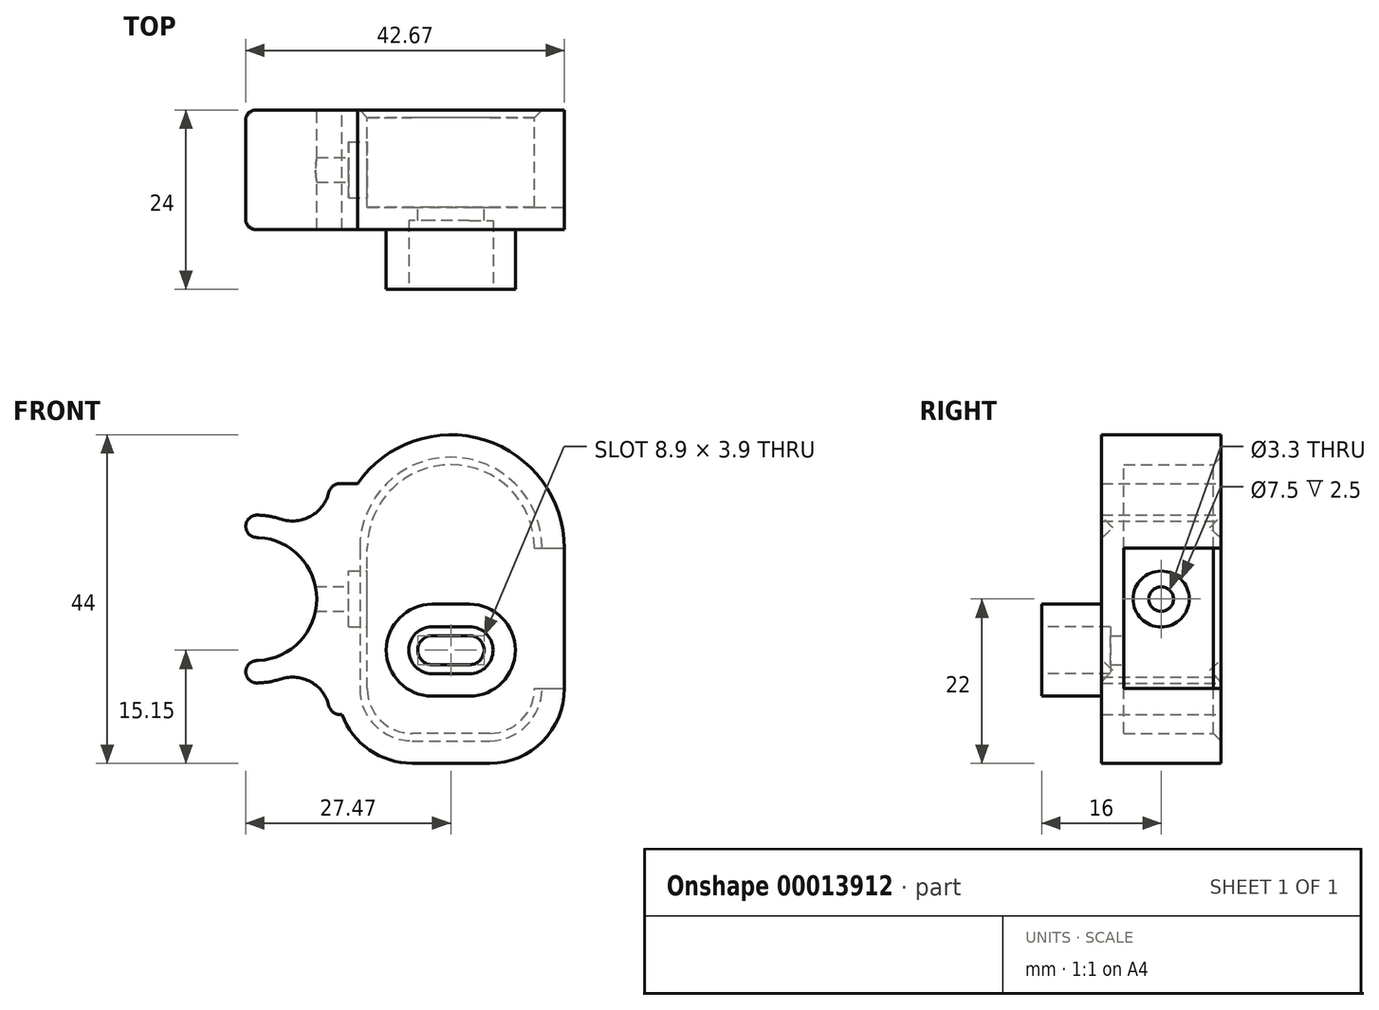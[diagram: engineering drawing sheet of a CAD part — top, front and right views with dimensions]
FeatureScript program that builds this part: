
annotation { "Feature Type Name" : "Feature", "Feature Type Description" : "" }
export const myFeature = defineFeature(function(context is Context, id is Id, definition is map)
    precondition{}
    {
        {
            var Q0;
            Q0=qCreatedBy(makeId("Front.planeOp"),FACE);
            var sketch = newSketch(context, id + "F0", { "sketchPlane" : qUnion([Q0])});
            skArc(sketch, "E0", {"start": v(-1.08, -8.18) * mm, "mid": v(8.25, 0) * mm, "end": v(-1.08, 8.18) * mm});
            skArc(sketch, "E1", {"start": v(3.46, 10.7) * mm, "mid": v(1.02, 11.2) * mm, "end": v(-1.47, 11.15) * mm});
            skLineSegment(sketch, "E2", {"start": v(-1.08, 8.18) * mm, "end": v(-1.47, 11.15) * mm});
            skLineSegment(sketch, "E3", {"start": v(-1.08, -8.18) * mm, "end": v(-1.47, -11.15) * mm});
            skLineSegment(sketch, "E4", {"start": v(0, 0) * mm, "end": v(-11.25, 0) * mm, "construction": true});
            skLineSegment(sketch, "E5", {"start": v(10, 15.46) * mm, "end": v(10, 15.46) * mm});
            skLineSegment(sketch, "E6", {"start": v(15, 0) * mm, "end": v(15, 15.46) * mm});
            skPoint(sketch, "E7.orphan", {"position": v(8.25, 0) * mm});
            skArc(sketch, "E8.trimOffspring", {"start": v(-1.47, -11.15) * mm, "mid": v(1.02, -11.2) * mm, "end": v(3.46, -10.7) * mm});
            skArc(sketch, "E9.filletArc", {"start": v(3.46, 10.7) * mm, "mid": v(7.94, 11.42) * mm, "end": v(10, 15.46) * mm});
            skLineSegment(sketch, "E10.MirrorCS", {"start": v(15, 0) * mm, "end": v(15, -15.46) * mm});
            skLineSegment(sketch, "E11", {"start": v(10, 15.46) * mm, "end": v(15, 15.46) * mm});
            skLineSegment(sketch, "E12.MirrorCS", {"start": v(10, -15.46) * mm, "end": v(15, -15.46) * mm});
            skArc(sketch, "E13.MirrorCS", {"start": v(3.46, -10.7) * mm, "mid": v(7.94, -11.42) * mm, "end": v(10, -15.46) * mm});
            skSolve(sketch);
        }
        {
            var Q0;
            Q0=qSketchRegion(id+"F0",true);
            extrude(context, id + "F1", {"entities" : qUnion([Q0]), "depth" : 8 * mm, "hasSecondDirection" : true, "secondDirectionOppositeDirection" : true, "secondDirectionDepth" : 8 * mm});
        }
        {
            var Q0;
            Q0=makeQuery(id+"F1.opExtrude","SWEPT_FACE",FACE,{"disambiguationData":[OSD([sQuery(id+"F0.wireOp",EDGE,"E6"),sQuery(id+"F0.wireOp",EDGE,"E10.MirrorCS")])]});
            var sketch = newSketch(context, id + "F2", { "sketchPlane" : qUnion([Q0])});
            skCircle(sketch, "E14", {"center": v(0, 0) * mm, "radius": 4 * mm});
            skSolve(sketch);
        }
        {
            var Q0;
            Q0=qSketchRegion(id+"F2",true);
            extrude(context, id + "F3", {"entities" : qUnion([Q0]), "operationType" : NewBodyOperationType.REMOVE, "oppositeDirection" : true, "depth" : 3 * mm});
        }
        {
            var Q0;
            Q0=makeQuery(id+"F1.opExtrude","SWEPT_FACE",FACE,{"disambiguationData":[OSD([sQuery(id+"F0.wireOp",EDGE,"E3")])]});
            var Q1;
            Q1=makeQuery(id+"F1.opExtrude","SWEPT_FACE",FACE,{"disambiguationData":[OSD([sQuery(id+"F0.wireOp",EDGE,"E2")])]});
            var Q2;
            Q2=makeQuery(id+"F1.opExtrude","SWEPT_EDGE",EDGE,{"disambiguationData":[OSD([sQuery(id+"F0.wireOp",EDGE,"E9.filletArc"),sQuery(id+"F0.wireOp",EDGE,"E11")])]});
            var Q3;
            Q3=makeQuery(id+"F1.opExtrude","SWEPT_EDGE",EDGE,{"disambiguationData":[OSD([sQuery(id+"F0.wireOp",EDGE,"E12.MirrorCS"),sQuery(id+"F0.wireOp",EDGE,"E13.MirrorCS")])]});
            fillet(context, id + "F4", {"entities" : qUnion([Q0, Q1, Q2, Q3]), "radius" : 1.5 * mm, "tangentPropagation" : true, "allowEdgeOverflow" : false});
        }
        {
            var Q0;
            Q0=qCreatedBy(makeId("Front.planeOp"),FACE);
            var sketch = newSketch(context, id + "F5", { "sketchPlane" : qUnion([Q0])});
            skLineSegment(sketch, "E15.1", {"start": v(15, 6.8) * mm, "end": v(15, -12) * mm});
            skArc(sketch, "E16", {"start": v(15, 6.8) * mm, "mid": v(26.2, 18) * mm, "end": v(37.4, 6.8) * mm});
            skArc(sketch, "E17", {"start": v(15, -12) * mm, "mid": v(16.76, -16.24) * mm, "end": v(21, -18) * mm});
            skLineSegment(sketch, "E18", {"start": v(21, -18) * mm, "end": v(31.4, -18) * mm});
            skArc(sketch, "E19", {"start": v(31.4, -18) * mm, "mid": v(35.64, -16.24) * mm, "end": v(37.4, -12) * mm});
            skLineSegment(sketch, "E20", {"start": v(26.2, 18) * mm, "end": v(0, 18) * mm, "construction": true});
            skLineSegment(sketch, "E21", {"start": v(0, 0) * mm, "end": v(15, 0) * mm, "construction": true});
            skArc(sketch, "E22.0", {"start": v(11, 6.8) * mm, "mid": v(26.2, 22) * mm, "end": v(41.4, 6.8) * mm});
            skLineSegment(sketch, "E23", {"start": v(37.4, 6.8) * mm, "end": v(41.4, 6.8) * mm});
            skArc(sketch, "E24.0", {"start": v(31.4, -22) * mm, "mid": v(38.47, -19.07) * mm, "end": v(41.4, -12) * mm});
            skLineSegment(sketch, "E24.1", {"start": v(21, -22) * mm, "end": v(31.4, -22) * mm});
            skArc(sketch, "E24.2", {"start": v(11, -12) * mm, "mid": v(13.93, -19.07) * mm, "end": v(21, -22) * mm});
            skLineSegment(sketch, "E25", {"start": v(11, 6.8) * mm, "end": v(11, -12) * mm});
            skLineSegment(sketch, "E26", {"start": v(37.4, -12) * mm, "end": v(41.4, -12) * mm});
            skSolve(sketch);
        }
        {
            var Q0;
            Q0 = qSketchRegion(id + "F5", true);
            var Q1;
            Q1=makeQuery(id+"F1.opExtrude","CAP_FACE",FACE,{"disambiguationData":[OSD([sQuery(id+"F0.wireOp",EDGE,"E0"),sQuery(id+"F0.wireOp",EDGE,"E1"),sQuery(id+"F0.wireOp",EDGE,"E2"),sQuery(id+"F0.wireOp",EDGE,"E3"),sQuery(id+"F0.wireOp",EDGE,"E6"),sQuery(id+"F0.wireOp",EDGE,"E8.trimOffspring"),sQuery(id+"F0.wireOp",EDGE,"E9.filletArc"),sQuery(id+"F0.wireOp",EDGE,"E10.MirrorCS"),sQuery(id+"F0.wireOp",EDGE,"E11"),sQuery(id+"F0.wireOp",EDGE,"E12.MirrorCS"),sQuery(id+"F0.wireOp",EDGE,"E13.MirrorCS")])],"isStart":false});
            var Q2;
            Q2=makeQuery(id+"F1.opExtrude","CAP_FACE",FACE,{"disambiguationData":[OSD([sQuery(id+"F0.wireOp",EDGE,"E0"),sQuery(id+"F0.wireOp",EDGE,"E1"),sQuery(id+"F0.wireOp",EDGE,"E2"),sQuery(id+"F0.wireOp",EDGE,"E3"),sQuery(id+"F0.wireOp",EDGE,"E6"),sQuery(id+"F0.wireOp",EDGE,"E8.trimOffspring"),sQuery(id+"F0.wireOp",EDGE,"E9.filletArc"),sQuery(id+"F0.wireOp",EDGE,"E10.MirrorCS"),sQuery(id+"F0.wireOp",EDGE,"E11"),sQuery(id+"F0.wireOp",EDGE,"E12.MirrorCS"),sQuery(id+"F0.wireOp",EDGE,"E13.MirrorCS")])],"isStart":true});
            extrude(context, id + "F6", {"entities" : qUnion([Q0]), "operationType" : NewBodyOperationType.ADD, "endBound" : BoundingType.UP_TO_SURFACE, "endBoundEntityFace" : qUnion([Q1]), "depth" : 25 * mm, "hasSecondDirection" : true, "secondDirectionBound" : SecondDirectionBoundingType.UP_TO_SURFACE, "secondDirectionOppositeDirection" : true, "secondDirectionBoundEntityFace" : qUnion([Q2]), "secondDirectionDepth" : 25 * mm});
        }
        {
            var Q0;
            Q0=makeQuery(id+"F1.opExtrude","SWEPT_FACE",FACE,{"disambiguationData":[OSD([sQuery(id+"F0.wireOp",EDGE,"E6"),sQuery(id+"F0.wireOp",EDGE,"E10.MirrorCS")])]});
            var sketch = newSketch(context, id + "F7", { "sketchPlane" : qUnion([Q0])});
            skCircle(sketch, "E27", {"center": v(0, 0) * mm, "radius": 1.65 * mm});
            skSolve(sketch);
        }
        {
            var Q0;
            Q0=qSketchRegion(id+"F7",true);
            var Q1;
            Q1=makeQuery(id+"F1.opExtrude","SWEPT_FACE",FACE,{"disambiguationData":[OSD([sQuery(id+"F0.wireOp",EDGE,"E6"),sQuery(id+"F0.wireOp",EDGE,"E10.MirrorCS")])]});
            extrude(context, id + "F8", {"entities" : qUnion([Q0]), "operationType" : NewBodyOperationType.REMOVE, "endBound" : BoundingType.THROUGH_ALL, "oppositeDirection" : true, "endBoundEntityFace" : qUnion([Q1]), "depth" : 25 * mm});
        }
        {
            var Q0;
            Q0=makeQuery(id+"F6.boolean.opBoolean","MERGE",FACE,{"derivedFrom":[makeQuery(id+"F1.opExtrude","CAP_FACE",FACE,{"disambiguationData":[OSD([sQuery(id+"F0.wireOp",EDGE,"E0"),sQuery(id+"F0.wireOp",EDGE,"E1"),sQuery(id+"F0.wireOp",EDGE,"E2"),sQuery(id+"F0.wireOp",EDGE,"E3"),sQuery(id+"F0.wireOp",EDGE,"E6"),sQuery(id+"F0.wireOp",EDGE,"E8.trimOffspring"),sQuery(id+"F0.wireOp",EDGE,"E9.filletArc"),sQuery(id+"F0.wireOp",EDGE,"E10.MirrorCS"),sQuery(id+"F0.wireOp",EDGE,"E11"),sQuery(id+"F0.wireOp",EDGE,"E12.MirrorCS"),sQuery(id+"F0.wireOp",EDGE,"E13.MirrorCS")])],"isStart":false}),makeQuery(id+"F6.opExtrude","CAP_FACE",FACE,{"disambiguationData":[OSD([sQuery(id+"F5.wireOp",EDGE,"E15.1"),sQuery(id+"F5.wireOp",EDGE,"E16"),sQuery(id+"F5.wireOp",EDGE,"E17"),sQuery(id+"F5.wireOp",EDGE,"E18"),sQuery(id+"F5.wireOp",EDGE,"E19"),sQuery(id+"F5.wireOp",EDGE,"E22.0"),sQuery(id+"F5.wireOp",EDGE,"E23"),sQuery(id+"F5.wireOp",EDGE,"E24.0"),sQuery(id+"F5.wireOp",EDGE,"E24.1"),sQuery(id+"F5.wireOp",EDGE,"E24.2"),sQuery(id+"F5.wireOp",EDGE,"E25"),sQuery(id+"F5.wireOp",EDGE,"E26")])],"isStart":false})]});
            var sketch = newSketch(context, id + "F9", { "sketchPlane" : qUnion([Q0])});
            skArc(sketch, "E28.0", {"start": v(11, 6.8) * mm, "mid": v(26.2, 22) * mm, "end": v(41.4, 6.8) * mm});
            skArc(sketch, "E29.0", {"start": v(31.4, -22) * mm, "mid": v(38.47, -19.07) * mm, "end": v(41.4, -12) * mm});
            skLineSegment(sketch, "E29.1", {"start": v(21, -22) * mm, "end": v(31.4, -22) * mm});
            skArc(sketch, "E29.2", {"start": v(11, -12) * mm, "mid": v(13.93, -19.07) * mm, "end": v(21, -22) * mm});
            skLineSegment(sketch, "E30", {"start": v(11, 6.8) * mm, "end": v(11, -12) * mm});
            skLineSegment(sketch, "E31", {"start": v(41.4, 6.8) * mm, "end": v(41.4, -12) * mm});
            skLineSegment(sketch, "E32.rect.bottom", {"start": v(28.7, -10) * mm, "end": v(23.7, -10) * mm});
            skLineSegment(sketch, "E32.rect.top", {"start": v(28.7, -3.7) * mm, "end": v(23.7, -3.7) * mm});
            skLineSegment(sketch, "E32.rect.left", {"start": v(28.7, -10) * mm, "end": v(28.7, -3.7) * mm, "construction": true});
            skLineSegment(sketch, "E32.rect.right", {"start": v(23.7, -10) * mm, "end": v(23.7, -3.7) * mm, "construction": true});
            skPoint(sketch, "E32.rect.middle", {"position": v(26.2, -6.85) * mm});
            skLineSegment(sketch, "E33", {"start": v(26.2, 6.8) * mm, "end": v(26.2, -6.85) * mm, "construction": true});
            skArc(sketch, "E34", {"start": v(23.7, -10) * mm, "mid": v(20.55, -6.85) * mm, "end": v(23.7, -3.7) * mm});
            skArc(sketch, "E35", {"start": v(28.7, -3.7) * mm, "mid": v(31.85, -6.85) * mm, "end": v(28.7, -10) * mm});
            skSolve(sketch);
        }
        {
            var Q0;
            Q0 = qSketchRegion(id + "F9", true);
            extrude(context, id + "F10", {"entities" : qUnion([Q0]), "operationType" : NewBodyOperationType.ADD, "oppositeDirection" : true, "depth" : 3 * mm});
        }
        {
            var Q0;
            Q0=makeQuery(id+"F6.boolean.opBoolean","MERGE",FACE,{"derivedFrom":[makeQuery(id+"F1.opExtrude","SWEPT_FACE",FACE,{"disambiguationData":[OSD([sQuery(id+"F0.wireOp",EDGE,"E6"),sQuery(id+"F0.wireOp",EDGE,"E10.MirrorCS")])]}),makeQuery(id+"F6.opExtrude","SWEPT_FACE",FACE,{"disambiguationData":[OSD([sQuery(id+"F5.wireOp",EDGE,"E15.1")])]})]});
            var sketch = newSketch(context, id + "F11", { "sketchPlane" : qUnion([Q0])});
            skCircle(sketch, "E36.0", {"center": v(0, 0) * mm, "radius": 3.75 * mm});
            skSolve(sketch);
        }
        {
            var Q0;
            Q0 = qSketchRegion(id + "F11", true);
            extrude(context, id + "F12", {"entities" : qUnion([Q0]), "operationType" : NewBodyOperationType.REMOVE, "oppositeDirection" : true, "depth" : 2.5 * mm});
        }
        {
            var Q0;
            Q0=makeQuery(id+"F10.boolean.opBoolean","MERGE",FACE,{"derivedFrom":[makeQuery(id+"F6.boolean.opBoolean","MERGE",FACE,{"derivedFrom":[makeQuery(id+"F1.opExtrude","CAP_FACE",FACE,{"disambiguationData":[OSD([sQuery(id+"F0.wireOp",EDGE,"E0"),sQuery(id+"F0.wireOp",EDGE,"E1"),sQuery(id+"F0.wireOp",EDGE,"E2"),sQuery(id+"F0.wireOp",EDGE,"E3"),sQuery(id+"F0.wireOp",EDGE,"E6"),sQuery(id+"F0.wireOp",EDGE,"E8.trimOffspring"),sQuery(id+"F0.wireOp",EDGE,"E9.filletArc"),sQuery(id+"F0.wireOp",EDGE,"E10.MirrorCS"),sQuery(id+"F0.wireOp",EDGE,"E11"),sQuery(id+"F0.wireOp",EDGE,"E12.MirrorCS"),sQuery(id+"F0.wireOp",EDGE,"E13.MirrorCS")])],"isStart":false}),makeQuery(id+"F6.opExtrude","CAP_FACE",FACE,{"disambiguationData":[OSD([sQuery(id+"F5.wireOp",EDGE,"E15.1"),sQuery(id+"F5.wireOp",EDGE,"E16"),sQuery(id+"F5.wireOp",EDGE,"E17"),sQuery(id+"F5.wireOp",EDGE,"E18"),sQuery(id+"F5.wireOp",EDGE,"E19"),sQuery(id+"F5.wireOp",EDGE,"E22.0"),sQuery(id+"F5.wireOp",EDGE,"E23"),sQuery(id+"F5.wireOp",EDGE,"E24.0"),sQuery(id+"F5.wireOp",EDGE,"E24.1"),sQuery(id+"F5.wireOp",EDGE,"E24.2"),sQuery(id+"F5.wireOp",EDGE,"E25"),sQuery(id+"F5.wireOp",EDGE,"E26")])],"isStart":false})]}),makeQuery(id+"F10.opExtrude","CAP_FACE",FACE,{"disambiguationData":[OSD([sQuery(id+"F9.wireOp",EDGE,"E28.0"),sQuery(id+"F9.wireOp",EDGE,"E29.0"),sQuery(id+"F9.wireOp",EDGE,"E29.1"),sQuery(id+"F9.wireOp",EDGE,"E29.2"),sQuery(id+"F9.wireOp",EDGE,"E30"),sQuery(id+"F9.wireOp",EDGE,"E31"),sQuery(id+"F9.wireOp",EDGE,"E32.rect.bottom"),sQuery(id+"F9.wireOp",EDGE,"E32.rect.top"),sQuery(id+"F9.wireOp",EDGE,"E34"),sQuery(id+"F9.wireOp",EDGE,"E35")])],"isStart":true})]});
            var sketch = newSketch(context, id + "F13", { "sketchPlane" : qUnion([Q0])});
            skArc(sketch, "E37.0", {"start": v(23.7, -10) * mm, "mid": v(20.55, -6.85) * mm, "end": v(23.7, -3.7) * mm});
            skLineSegment(sketch, "E38.0", {"start": v(28.7, -3.7) * mm, "end": v(23.7, -3.7) * mm});
            skArc(sketch, "E38.1", {"start": v(28.7, -3.7) * mm, "mid": v(31.85, -6.85) * mm, "end": v(28.7, -10) * mm});
            skLineSegment(sketch, "E38.2", {"start": v(28.7, -10) * mm, "end": v(23.7, -10) * mm});
            skArc(sketch, "E39.0", {"start": v(28.7, -0.7) * mm, "mid": v(34.85, -6.85) * mm, "end": v(28.7, -13) * mm});
            skLineSegment(sketch, "E39.1", {"start": v(28.7, -0.7) * mm, "end": v(23.7, -0.7) * mm});
            skArc(sketch, "E39.2", {"start": v(23.7, -13) * mm, "mid": v(17.55, -6.85) * mm, "end": v(23.7, -0.7) * mm});
            skLineSegment(sketch, "E39.3", {"start": v(28.7, -13) * mm, "end": v(23.7, -13) * mm});
            skSolve(sketch);
        }
        {
            var Q0;
            Q0 = qSketchRegion(id + "F13", true);
            extrude(context, id + "F14", {"entities" : qUnion([Q0]), "operationType" : NewBodyOperationType.ADD, "depth" : 8 * mm});
        }
        {
            var Q0;
            Q0=makeQuery(id+"F10.opExtrude","CAP_FACE",FACE,{"disambiguationData":[OSD([sQuery(id+"F9.wireOp",EDGE,"E28.0"),sQuery(id+"F9.wireOp",EDGE,"E29.0"),sQuery(id+"F9.wireOp",EDGE,"E29.1"),sQuery(id+"F9.wireOp",EDGE,"E29.2"),sQuery(id+"F9.wireOp",EDGE,"E30"),sQuery(id+"F9.wireOp",EDGE,"E31"),sQuery(id+"F9.wireOp",EDGE,"E32.rect.bottom"),sQuery(id+"F9.wireOp",EDGE,"E32.rect.top"),sQuery(id+"F9.wireOp",EDGE,"E34"),sQuery(id+"F9.wireOp",EDGE,"E35")])],"isStart":false});
            var sketch = newSketch(context, id + "F15", { "sketchPlane" : qUnion([Q0])});
            skArc(sketch, "E40.0", {"start": v(-23.7, -10) * mm, "mid": v(-20.55, -6.85) * mm, "end": v(-23.7, -3.7) * mm});
            skLineSegment(sketch, "E40.1", {"start": v(-28.7, -3.7) * mm, "end": v(-23.7, -3.7) * mm});
            skArc(sketch, "E40.2", {"start": v(-28.7, -3.7) * mm, "mid": v(-31.85, -6.85) * mm, "end": v(-28.7, -10) * mm});
            skLineSegment(sketch, "E40.3", {"start": v(-28.7, -10) * mm, "end": v(-23.7, -10) * mm});
            skArc(sketch, "E41.0", {"start": v(-23.7, -8.8) * mm, "mid": v(-21.75, -6.85) * mm, "end": v(-23.7, -4.9) * mm});
            skLineSegment(sketch, "E41.1", {"start": v(-28.7, -8.8) * mm, "end": v(-23.7, -8.8) * mm});
            skArc(sketch, "E41.2", {"start": v(-28.7, -4.9) * mm, "mid": v(-30.65, -6.85) * mm, "end": v(-28.7, -8.8) * mm});
            skLineSegment(sketch, "E41.3", {"start": v(-28.7, -4.9) * mm, "end": v(-23.7, -4.9) * mm});
            skSolve(sketch);
        }
        {
            var Q0;
            Q0 = qSketchRegion(id + "F15", true);
            extrude(context, id + "F16", {"entities" : qUnion([Q0]), "operationType" : NewBodyOperationType.ADD, "oppositeDirection" : true, "depth" : 1.8 * mm});
        }
        {
            var Q0;
            Q0=makeQuery(id+"F6.opExtrude","CAP_EDGE",EDGE,{"disambiguationData":[OSD([sQuery(id+"F5.wireOp",EDGE,"E16")])],"isStart":true});
            var Q1;
            Q1=makeQuery(id+"F1.opExtrude","CAP_EDGE",EDGE,{"disambiguationData":[OSD([sQuery(id+"F0.wireOp",EDGE,"E6"),sQuery(id+"F0.wireOp",EDGE,"E10.MirrorCS")])],"isStart":true});
            var Q2;
            Q2=makeQuery(id+"F6.opExtrude","CAP_EDGE",EDGE,{"disambiguationData":[OSD([sQuery(id+"F5.wireOp",EDGE,"E17")])],"isStart":true});
            var Q3;
            Q3=makeQuery(id+"F6.opExtrude","CAP_EDGE",EDGE,{"disambiguationData":[OSD([sQuery(id+"F5.wireOp",EDGE,"E18")])],"isStart":true});
            var Q4;
            Q4=makeQuery(id+"F6.opExtrude","CAP_EDGE",EDGE,{"disambiguationData":[OSD([sQuery(id+"F5.wireOp",EDGE,"E19")])],"isStart":true});
            chamfer(context, id + "F17", {"entities" : qUnion([Q0, Q1, Q2, Q3, Q4]), "width" : 1 * mm, "tangentPropagation" : true});
        }
    });
